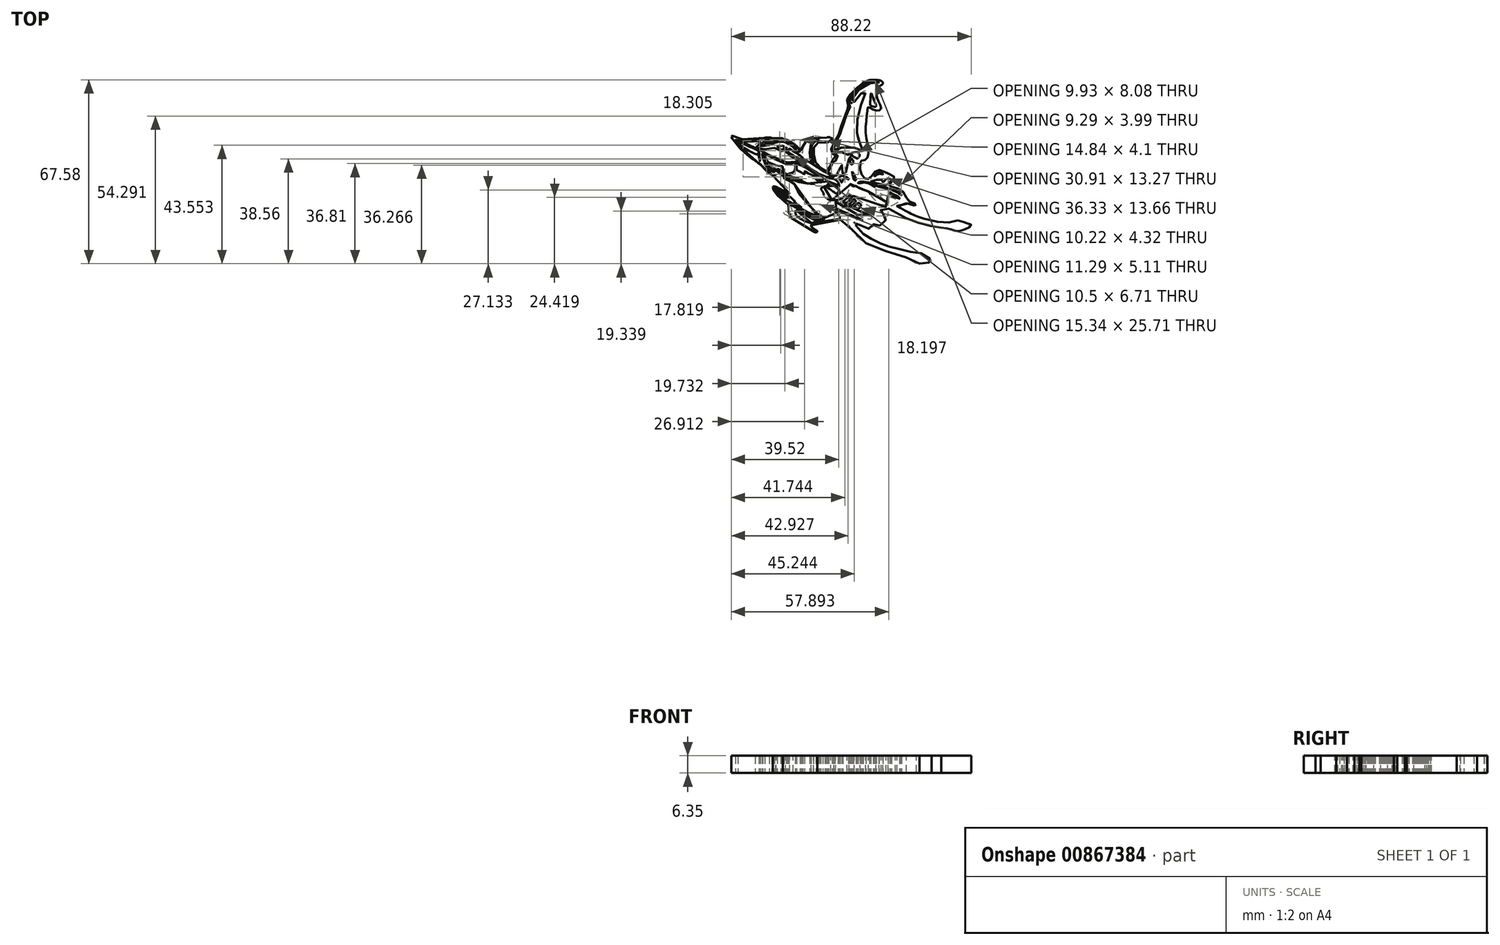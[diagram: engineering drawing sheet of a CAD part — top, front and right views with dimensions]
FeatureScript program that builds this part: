
annotation { "Feature Type Name" : "Feature", "Feature Type Description" : "" }
export const myFeature = defineFeature(function(context is Context, id is Id, definition is map)
    precondition{}
    {
        {
            var Q0;
            Q0=qCreatedBy(makeId("Top.planeOp"),FACE);
            var sketch = newSketch(context, id + "F0", { "sketchPlane" : qUnion([Q0])});
            skFitSpline(sketch, "E0", {"points": [v(41.98, 48.6) * mm, v(43.9, 48.97) * mm, v(44.37, 48.91) * mm, v(44.52, 48.63) * mm, v(44.44, 48.26) * mm, v(44.15, 47.9) * mm, v(43.74, 47.62) * mm, v(42.93, 47.19) * mm, v(42.29, 46.82) * mm, v(42.06, 46.82) * mm, v(40.95, 46.8) * mm, v(39.6, 46.76) * mm, v(38.49, 46.64) * mm, v(38.07, 46.36) * mm, v(37.56, 45.85) * mm, v(37.26, 45.35) * mm, v(37.13, 44.9) * mm, v(37.04, 44.36) * mm, v(37.01, 43.72) * mm, v(37, 42.9) * mm, v(37.17, 41.97) * mm, v(37.41, 41.22) * mm, v(37.56, 40.41) * mm, v(37.68, 39.64) * mm, v(37.94, 38.93) * mm, v(38.5, 38.27) * mm, v(39.2, 37.71) * mm, v(39.97, 37.17) * mm, v(40.53, 36.8) * mm, v(41.1, 36.43) * mm, v(41.55, 36.15) * mm, v(41.7, 36.05) * mm, v(41.86, 36.05) * mm, v(41.98, 36.19) * mm, v(42.32, 36.67) * mm, v(43.09, 38) * mm, v(43.48, 38.84) * mm, v(43.73, 39.67) * mm, v(43.85, 40.2) * mm, v(43.95, 40.42) * mm, v(44.07, 40.53) * mm, v(44.25, 40.59) * mm, v(44.44, 40.57) * mm, v(44.68, 40.66) * mm, v(44.9, 40.88) * mm, v(45.08, 41.2) * mm, v(45.14, 41.5) * mm, v(45.1, 41.77) * mm, v(44.95, 42.01) * mm, v(44.72, 42.23) * mm, v(44.54, 42.34) * mm, v(44.36, 42.38) * mm, v(44.25, 42.44) * mm, v(44, 42.65) * mm, v(43.84, 42.84) * mm, v(43.48, 43.12) * mm, v(43.35, 43.2) * mm, v(43.39, 43.45) * mm, v(43.48, 43.85) * mm, v(43.57, 44.25) * mm, v(44.01, 45.4) * mm, v(44.39, 46.2) * mm, v(44.73, 46.9) * mm, v(45.15, 47.64) * mm, v(45.68, 48.6) * mm, v(46.04, 49.27) * mm, v(46.33, 49.92) * mm, v(46.48, 50.56) * mm, v(46.91, 51.88) * mm, v(47.29, 52.96) * mm, v(47.67, 53.81) * mm, v(48.05, 54.9) * mm, v(48.34, 55.82) * mm, v(48.7, 56.96) * mm, v(49.23, 58.28) * mm, v(49.6, 59.15) * mm, v(49.93, 59.76) * mm, v(50.1, 60.04) * mm, v(50.13, 60.13) * mm, v(50.08, 60.23) * mm, v(49.9, 60.42) * mm, v(49.81, 60.56) * mm, v(49.53, 60.97) * mm, v(49.44, 61.13) * mm, v(49.4, 61.27) * mm, v(49.36, 61.68) * mm, v(49.37, 62.12) * mm, v(49.38, 62.52) * mm, v(49.48, 62.86) * mm, v(49.7, 63.3) * mm, v(50.14, 63.88) * mm, v(50.55, 64.34) * mm, v(51.4, 65.2) * mm, v(52.13, 65.94) * mm, v(52.85, 66.69) * mm, v(53.39, 67.22) * mm, v(53.94, 67.76) * mm, v(54.36, 68.08) * mm, v(55.06, 68.47) * mm], "startDerivative": vector(117.58, 26) * mm, "endDerivative": vector(61.76, 33.34) * mm});
            skFitSpline(sketch, "E1", {"points": [v(55.06, 68.47) * mm, v(55.59, 68.8) * mm, v(56.05, 69.09) * mm, v(56.53, 69.34) * mm, v(57.02, 69.52) * mm, v(57.43, 69.66) * mm, v(57.78, 69.7) * mm, v(58.18, 69.74) * mm, v(58.9, 69.73) * mm, v(59.55, 69.72) * mm, v(60.32, 69.7) * mm, v(61.28, 69.62) * mm, v(61.67, 69.5) * mm, v(61.99, 69.32) * mm, v(62.26, 69.08) * mm, v(62.43, 68.88) * mm, v(62.5, 68.77) * mm, v(62.52, 68.62) * mm, v(62.52, 68.43) * mm, v(62.48, 68.3) * mm, v(62.4, 68.17) * mm, v(62.22, 68.02) * mm, v(62.06, 67.9) * mm, v(61.9, 67.8) * mm, v(61.7, 67.69) * mm, v(61.54, 67.59) * mm, v(61.4, 67.5) * mm, v(61.17, 67.37) * mm, v(61, 67.26) * mm, v(60.79, 67.13) * mm, v(60.6, 66.97) * mm, v(60.47, 66.85) * mm, v(60.3, 66.68) * mm, v(60.16, 66.48) * mm, v(60.08, 66.3) * mm, v(60, 66.01) * mm], "startDerivative": vector(13.49, 8.7) * mm, "endDerivative": vector(-3.18, -11.09) * mm});
            skFitSpline(sketch, "E2", {"points": [v(58.3, 64.82) * mm, v(58.43, 64.52) * mm, v(58.67, 63.82) * mm, v(58.93, 63.08) * mm, v(59.33, 62) * mm, v(59.67, 61.3) * mm, v(60.07, 60.52) * mm, v(60.14, 60.21) * mm, v(60, 59.97) * mm, v(59.8, 59.88) * mm, v(59.3, 59.86) * mm, v(58.85, 59.98) * mm, v(58.4, 60.17) * mm, v(57.95, 60.44) * mm, v(57.82, 60.59) * mm, v(57.78, 60.94) * mm, v(57.9, 61.76) * mm, v(57.96, 62.72) * mm, v(58, 63.73) * mm, v(58.07, 64.4) * mm, v(58.14, 64.66) * mm, v(58.18, 64.78) * mm, v(58.3, 64.82) * mm]});
            skFitSpline(sketch, "E3", {"points": [v(55.21, 43.64) * mm, v(55.24, 44.2) * mm, v(55.08, 44.77) * mm, v(54.83, 45.45) * mm, v(54.48, 46.03) * mm, v(54.03, 46.77) * mm, v(53.69, 47.3) * mm, v(53.4, 47.93) * mm, v(53.24, 48.48) * mm, v(53.13, 49.1) * mm, v(53, 49.95) * mm, v(52.96, 50.59) * mm, v(52.92, 52.06) * mm, v(52.93, 53.55) * mm, v(53.06, 54.95) * mm, v(53.33, 56.48) * mm, v(53.76, 58.41) * mm, v(54.17, 59.75) * mm, v(54.6, 60.97) * mm, v(55.07, 62.3) * mm, v(55.72, 63.92) * mm, v(55.96, 64.35) * mm, v(56.2, 65.04) * mm, v(56.3, 65.47) * mm, v(56.27, 65.67) * mm, v(56.04, 65.75) * mm, v(55.8, 65.66) * mm, v(55.4, 65.43) * mm, v(54.82, 65.01) * mm, v(54.12, 64.39) * mm, v(53.53, 63.73) * mm, v(52.83, 62.85) * mm, v(52.33, 62.13) * mm, v(51.81, 61.5) * mm, v(51.34, 61.23) * mm, v(51.06, 61.18) * mm, v(50.84, 61.28) * mm, v(50.71, 61.48) * mm, v(50.84, 61.87) * mm, v(51.09, 62.32) * mm, v(51.48, 62.95) * mm, v(51.94, 63.63) * mm, v(52.34, 64.22) * mm, v(53.1, 65.33) * mm, v(53.88, 66.29) * mm, v(54.81, 67.24) * mm, v(55.98, 68.08) * mm, v(56.93, 68.42) * mm, v(58.16, 68.54) * mm, v(59.23, 68.55) * mm, v(59.7, 68.46) * mm, v(60.42, 68.52) * mm, v(60.87, 68.66) * mm, v(61.08, 68.76) * mm, v(61.08, 68.88) * mm, v(60.98, 69.01) * mm, v(60.39, 69.17) * mm, v(59.5, 69.32) * mm, v(58.18, 69.2) * mm, v(57.02, 68.88) * mm, v(55.92, 68.46) * mm, v(55.55, 68.26) * mm, v(54.99, 67.95) * mm, v(54.67, 67.72) * mm, v(53.94, 67.13) * mm, v(53.3, 66.48) * mm, v(52.68, 65.85) * mm, v(52.02, 65.17) * mm, v(51.74, 64.88) * mm, v(51.09, 64.15) * mm, v(50.5, 63.44) * mm, v(50.11, 62.82) * mm, v(49.98, 62.5) * mm, v(49.87, 61.78) * mm, v(49.9, 61.38) * mm, v(50, 61.1) * mm, v(50.54, 60.42) * mm, v(50.67, 60.13) * mm, v(50.67, 60.03) * mm, v(50.54, 59.88) * mm, v(50.3, 59.58) * mm, v(50.12, 59.3) * mm, v(49.73, 58.28) * mm, v(49.36, 57.33) * mm, v(48.91, 56.23) * mm, v(48.62, 55.32) * mm, v(48.36, 54.43) * mm, v(48.13, 53.78) * mm, v(47.8, 52.92) * mm, v(47.33, 51.68) * mm, v(47.02, 50.78) * mm, v(46.82, 49.96) * mm, v(46.32, 48.78) * mm, v(45.52, 47.37) * mm, v(45.1, 46.63) * mm, v(44.52, 45.44) * mm, v(44.04, 44.25) * mm, v(43.86, 43.45) * mm, v(43.89, 43.32) * mm, v(44.04, 43.34) * mm, v(44.28, 43.54) * mm, v(44.6, 43.78) * mm, v(44.94, 44.05) * mm, v(45.78, 44.4) * mm, v(46.69, 44.7) * mm, v(47.67, 44.96) * mm, v(48.57, 45.13) * mm, v(49.81, 45.12) * mm, v(51.28, 44.99) * mm, v(52.27, 44.73) * mm, v(52.95, 44.55) * mm, v(53.91, 44.17) * mm, v(54.47, 43.9) * mm, v(54.86, 43.7) * mm, v(55.21, 43.64) * mm]});
            skFitSpline(sketch, "E4", {"points": [v(60, 66.01) * mm, v(60, 65.43) * mm, v(60.12, 64.57) * mm, v(60.24, 63.95) * mm, v(60.5, 63.08) * mm, v(60.74, 62.35) * mm, v(61.04, 61.6) * mm, v(61.36, 60.87) * mm, v(61.66, 60.16) * mm, v(61.9, 59.48) * mm, v(61.92, 58.98) * mm, v(61.64, 58.7) * mm, v(61.25, 58.5) * mm, v(60.88, 58.44) * mm, v(60.34, 58.47) * mm, v(60, 58.52) * mm, v(59.22, 58.76) * mm, v(58.39, 59.16) * mm, v(57.58, 59.55) * mm, v(57.16, 59.73) * mm, v(57.02, 59.74) * mm, v(56.94, 59.68) * mm, v(56.9, 59.39) * mm, v(56.86, 58.84) * mm, v(56.76, 58.05) * mm, v(56.64, 56.68) * mm, v(56.46, 55.36) * mm, v(56.33, 53.9) * mm, v(56.2, 51.87) * mm, v(56.23, 50.08) * mm, v(56.37, 48.56) * mm, v(56.61, 47.28) * mm, v(56.9, 46.13) * mm, v(57.16, 44.6) * mm, v(57.23, 43.04) * mm, v(57.13, 41.88) * mm, v(56.92, 41.26) * mm, v(56.44, 40.67) * mm, v(55.95, 40.28) * mm, v(55.33, 40.08) * mm, v(54.79, 40.06) * mm, v(54.31, 40.03) * mm, v(54.27, 39.86) * mm, v(54.24, 39.46) * mm], "startDerivative": vector(-1.15, -26.38) * mm, "endDerivative": vector(-2.88, -24.95) * mm});
            skFitSpline(sketch, "E5", {"points": [v(44.86, 43.01) * mm, v(45.21, 43.13) * mm, v(46.25, 43.18) * mm, v(47.33, 43.12) * mm, v(48.31, 42.85) * mm, v(49.12, 42.58) * mm, v(49.7, 42.26) * mm, v(49.8, 42.15) * mm, v(49.99, 42.17) * mm, v(50.36, 42.4) * mm, v(50.83, 42.7) * mm, v(51.4, 42.97) * mm, v(51.95, 43.15) * mm, v(52.44, 43.28) * mm, v(52.89, 43.32) * mm, v(53.4, 43.25) * mm, v(53.81, 42.92) * mm, v(54.04, 42.58) * mm, v(54.13, 42.24) * mm, v(54.13, 41.83) * mm, v(54, 41.42) * mm, v(53.81, 41.13) * mm, v(53.51, 40.92) * mm, v(53.22, 40.8) * mm, v(52.8, 40.8) * mm, v(52.45, 40.87) * mm, v(52.08, 41.07) * mm, v(51.78, 41.41) * mm, v(51.63, 41.75) * mm, v(51.59, 42.16) * mm, v(51.58, 42.39) * mm, v(51.53, 42.47) * mm, v(51.38, 42.43) * mm, v(51.17, 42.26) * mm, v(50.92, 42) * mm, v(50.7, 41.76) * mm, v(50.5, 41.5) * mm, v(50.32, 41.13) * mm, v(50.06, 40.52) * mm, v(49.85, 39.8) * mm, v(49.6, 38.88) * mm, v(49.44, 37.97) * mm, v(49.27, 37.05) * mm, v(49.1, 36.23) * mm, v(48.95, 35.73) * mm, v(48.74, 35.2) * mm, v(48.51, 35) * mm, v(48.18, 34.95) * mm, v(47.86, 35) * mm, v(47.61, 35.3) * mm, v(47.45, 35.68) * mm, v(47.39, 36.33) * mm, v(47.55, 36.93) * mm, v(47.7, 37.52) * mm, v(47.74, 38.07) * mm, v(47.65, 38.4) * mm, v(47.54, 38.47) * mm, v(47.3, 38.23) * mm, v(47, 37.62) * mm, v(46.66, 36.98) * mm, v(46.45, 36.58) * mm, v(46.14, 35.9) * mm, v(45.93, 35.5) * mm, v(45.56, 34.7) * mm, v(45.34, 34.25) * mm, v(45.25, 34.14) * mm, v(45.08, 34.16) * mm, v(44.82, 34.29) * mm, v(44.18, 34.6) * mm, v(43.57, 34.92) * mm, v(42.98, 35.27) * mm, v(42.57, 35.52) * mm, v(42.3, 35.7) * mm, v(42.23, 35.8) * mm, v(42.4, 36.05) * mm, v(42.79, 36.67) * mm, v(43.2, 37.4) * mm, v(43.55, 38.02) * mm, v(43.78, 38.44) * mm, v(43.9, 38.95) * mm, v(44.05, 39.41) * mm, v(44.17, 39.72) * mm, v(44.32, 39.9) * mm, v(44.54, 40) * mm, v(44.95, 40.03) * mm, v(45.32, 40.16) * mm, v(45.73, 40.56) * mm, v(45.97, 41.04) * mm, v(46, 41.53) * mm, v(45.9, 41.95) * mm, v(45.65, 42.38) * mm, v(45.3, 42.72) * mm, v(45.03, 42.88) * mm, v(44.86, 43.01) * mm]});
            skFitSpline(sketch, "E6", {"points": [v(50.81, 40.97) * mm, v(51.07, 40.76) * mm, v(51.37, 40.32) * mm, v(51.61, 39.93) * mm, v(51.69, 39.46) * mm, v(51.67, 39.07) * mm, v(51.53, 38.94) * mm, v(51.32, 38.76) * mm, v(51.13, 38.66) * mm, v(50.92, 38.66) * mm, v(50.7, 38.92) * mm, v(50.57, 39.35) * mm, v(50.53, 39.9) * mm, v(50.6, 40.38) * mm, v(50.65, 40.7) * mm, v(50.72, 40.9) * mm, v(50.81, 40.97) * mm]});
            skFitSpline(sketch, "E7", {"points": [v(51.25, 36.03) * mm, v(51.52, 35.68) * mm, v(51.85, 35.08) * mm, v(52.2, 34.41) * mm, v(52.5, 33.68) * mm, v(52.63, 33.3) * mm, v(52.63, 32.93) * mm, v(52.45, 32.8) * mm, v(52.26, 32.8) * mm, v(52.02, 32.85) * mm, v(51.83, 33.1) * mm, v(51.67, 33.49) * mm, v(51.56, 34.07) * mm, v(51.44, 34.7) * mm, v(51.33, 35.4) * mm, v(51.2, 35.86) * mm, v(51.25, 36.03) * mm]});
            skFitSpline(sketch, "E8", {"points": [v(46.22, 33.81) * mm, v(46.48, 34.06) * mm, v(47.08, 34.34) * mm, v(47.61, 34.4) * mm, v(48.35, 34.27) * mm, v(49.08, 34.03) * mm, v(49.44, 33.87) * mm, v(49.78, 33.56) * mm, v(49.92, 33.35) * mm, v(49.98, 33.17) * mm, v(49.94, 33.1) * mm, v(49.73, 33.22) * mm, v(49.44, 33.41) * mm, v(49.06, 33.55) * mm, v(48.57, 33.54) * mm, v(48.2, 33.39) * mm, v(47.94, 33.18) * mm, v(47.7, 32.85) * mm, v(47.55, 32.49) * mm, v(47.55, 32.24) * mm, v(47.45, 32) * mm, v(47.32, 32) * mm, v(47.23, 32.2) * mm, v(47.13, 32.44) * mm, v(46.97, 32.71) * mm, v(46.77, 32.98) * mm, v(46.5, 33.33) * mm, v(46.31, 33.53) * mm, v(46.23, 33.65) * mm, v(46.22, 33.81) * mm]});
            skFitSpline(sketch, "E9", {"points": [v(54.24, 39.46) * mm, v(54.15, 38.57) * mm, v(54.15, 37.55) * mm, v(54.18, 36.68) * mm, v(54.28, 36.16) * mm, v(54.38, 35.7) * mm, v(54.6, 35.16) * mm, v(54.87, 34.66) * mm, v(55.14, 34.25) * mm, v(55.43, 33.9) * mm, v(55.8, 33.52) * mm, v(56.14, 33.2) * mm, v(56.34, 33.08) * mm, v(56.63, 33.06) * mm, v(56.99, 33.18) * mm, v(57.36, 33.36) * mm, v(57.65, 33.6) * mm, v(57.9, 33.82) * mm, v(58.14, 34.08) * mm, v(58.53, 34.57) * mm, v(58.91, 35.13) * mm, v(59.3, 35.63) * mm, v(59.66, 35.98) * mm, v(60.1, 36.33) * mm, v(60.5, 36.52) * mm, v(60.94, 36.62) * mm, v(61.36, 36.64) * mm, v(61.97, 36.59) * mm, v(62.68, 36.27) * mm, v(63.08, 35.94) * mm, v(63.41, 35.53) * mm, v(63.58, 35.32) * mm, v(63.92, 35.33) * mm, v(64.34, 35.3) * mm, v(65.05, 35.06) * mm, v(65.74, 34.72) * mm, v(66.5, 34.3) * mm, v(67, 33.89) * mm, v(67.08, 33.75) * mm, v(66.99, 33.52) * mm, v(66.74, 33.25) * mm, v(66.37, 32.84) * mm, v(65.95, 32.42) * mm, v(65.5, 31.97) * mm, v(65.02, 31.47) * mm, v(64.74, 31.17) * mm, v(64.49, 30.88) * mm, v(64.8, 30.76) * mm, v(65.16, 30.68) * mm, v(65.52, 30.56) * mm, v(66.57, 30.26) * mm, v(67.8, 29.87) * mm, v(68.68, 29.57) * mm, v(69.76, 28.8) * mm, v(70.46, 27.9) * mm, v(70.97, 27.09) * mm, v(71.18, 26.64) * mm, v(71.22, 25.86) * mm, v(71.26, 25.5) * mm, v(71.7, 25.25) * mm, v(72.42, 25.06) * mm, v(73.1, 24.8) * mm, v(73.9, 24.47) * mm, v(74.63, 24.01) * mm, v(74.83, 23.66) * mm, v(74.78, 23.48) * mm, v(74.47, 23.4) * mm, v(74.18, 23.48) * mm, v(73.5, 23.73) * mm, v(72.82, 23.95) * mm, v(71.9, 24.2) * mm, v(71.09, 24.27) * mm, v(70.46, 24.07) * mm, v(69.71, 23.82) * mm, v(69.02, 23.64) * mm, v(68.47, 23.53) * mm, v(68.09, 23.45) * mm, v(67.8, 23.4) * mm, v(67.73, 23.35) * mm, v(67.95, 23.15) * mm, v(68.29, 22.98) * mm, v(68.61, 22.85) * mm, v(68.96, 22.7) * mm], "startDerivative": vector(-7.45, -55.61) * mm, "endDerivative": vector(33.73, -15.96) * mm});
            skFitSpline(sketch, "E10", {"points": [v(60.87, 35.68) * mm, v(61.14, 35.7) * mm, v(61.66, 35.69) * mm, v(62.06, 35.58) * mm, v(62.32, 35.45) * mm, v(62.48, 35.27) * mm, v(62.57, 35.13) * mm, v(62.55, 34.97) * mm, v(62.34, 34.98) * mm, v(62.04, 35.1) * mm, v(61.66, 35.19) * mm, v(61.2, 35.19) * mm, v(60.85, 35.1) * mm, v(60.52, 34.97) * mm, v(60.24, 34.81) * mm, v(60.02, 34.66) * mm, v(59.78, 34.5) * mm, v(59.58, 34.37) * mm, v(59.4, 34.33) * mm, v(59.4, 34.44) * mm, v(59.61, 34.74) * mm, v(59.9, 35.07) * mm, v(60.13, 35.33) * mm, v(60.36, 35.5) * mm, v(60.64, 35.63) * mm, v(60.87, 35.68) * mm]});
            skFitSpline(sketch, "E11", {"points": [v(63.93, 31.08) * mm, v(64.34, 31.44) * mm, v(64.74, 31.82) * mm, v(65.27, 32.34) * mm, v(65.6, 32.69) * mm, v(65.74, 32.87) * mm, v(65.72, 33.05) * mm, v(65.49, 33.21) * mm, v(65.23, 33.34) * mm, v(64.88, 33.44) * mm, v(64.56, 33.48) * mm, v(64.16, 33.46) * mm, v(63.85, 33.36) * mm, v(63.55, 33.12) * mm, v(63.32, 32.86) * mm, v(63.12, 32.57) * mm, v(63, 32.34) * mm, v(62.84, 32.21) * mm, v(62.67, 32.16) * mm, v(62.46, 32.2) * mm, v(62.33, 32.3) * mm, v(62.25, 32.5) * mm, v(62.23, 32.76) * mm, v(62.2, 32.92) * mm, v(62.14, 33.01) * mm, v(62.05, 33.08) * mm, v(61.79, 33.11) * mm, v(61.26, 33.1) * mm, v(60.51, 33) * mm, v(59.83, 32.87) * mm, v(59.18, 32.73) * mm, v(58.5, 32.56) * mm, v(58.1, 32.46) * mm, v(58.09, 32.37) * mm, v(58.58, 32.14) * mm, v(59.28, 31.94) * mm, v(60.2, 31.7) * mm, v(61.37, 31.47) * mm, v(62.18, 31.3) * mm, v(63.15, 31.11) * mm, v(63.64, 31.04) * mm, v(63.93, 31.08) * mm]});
            skFitSpline(sketch, "E12", {"points": [v(53.59, 32) * mm, v(54.05, 32.18) * mm, v(54.66, 32.3) * mm, v(55.39, 32.32) * mm, v(56.1, 32.25) * mm, v(56.91, 32.09) * mm, v(57.75, 31.89) * mm, v(58.38, 31.66) * mm, v(58.82, 31.43) * mm, v(59.19, 31.12) * mm, v(59.44, 30.81) * mm, v(59.6, 30.56) * mm, v(59.67, 30.37) * mm, v(59.66, 30.27) * mm, v(59.5, 30.32) * mm, v(59.24, 30.48) * mm, v(58.9, 30.73) * mm, v(58.59, 30.96) * mm, v(58.16, 31.23) * mm, v(57.73, 31.46) * mm, v(57.2, 31.72) * mm, v(56.68, 31.86) * mm, v(56.17, 31.98) * mm, v(55.66, 31.97) * mm, v(55, 31.9) * mm, v(54.47, 31.84) * mm, v(54, 31.76) * mm, v(53.57, 31.76) * mm, v(53.4, 31.77) * mm, v(53.4, 31.86) * mm, v(53.5, 31.95) * mm, v(53.59, 32) * mm]});
            skFitSpline(sketch, "E13", {"points": [v(61.98, 30.88) * mm, v(62.53, 30.68) * mm, v(63.48, 30.25) * mm, v(64.45, 29.88) * mm, v(65.55, 29.53) * mm, v(66.52, 29.22) * mm, v(67.54, 28.85) * mm, v(68.43, 28.35) * mm, v(69.24, 27.61) * mm, v(69.46, 27.34) * mm, v(69.4, 27.26) * mm, v(69.3, 27.33) * mm, v(68.99, 27.59) * mm, v(68.45, 28.01) * mm, v(67.6, 28.48) * mm, v(66.86, 28.82) * mm, v(66.04, 29.17) * mm, v(65.1, 29.47) * mm, v(63.89, 29.8) * mm, v(62.47, 30.13) * mm, v(61.5, 30.32) * mm, v(60.75, 30.53) * mm, v(60.16, 30.82) * mm, v(59.79, 31.2) * mm, v(59.74, 31.3) * mm, v(59.8, 31.34) * mm, v(59.94, 31.3) * mm, v(60.38, 31.2) * mm, v(60.84, 31.1) * mm, v(61.33, 30.99) * mm, v(61.67, 30.92) * mm, v(61.98, 30.88) * mm]});
            skFitSpline(sketch, "E14", {"points": [v(65.16, 28.5) * mm, v(65.96, 27.97) * mm, v(67.04, 27.39) * mm, v(67.93, 26.89) * mm, v(68.38, 26.56) * mm, v(68.66, 26.3) * mm, v(68.7, 26.13) * mm, v(68.66, 26.07) * mm, v(68.32, 26.14) * mm, v(67.68, 26.38) * mm, v(66.93, 26.62) * mm, v(66.4, 26.83) * mm, v(65.92, 27) * mm, v(65.68, 27.15) * mm, v(65.6, 27.29) * mm, v(65.6, 27.47) * mm, v(65.49, 27.68) * mm, v(65.3, 27.99) * mm, v(65.14, 28.24) * mm, v(65.08, 28.4) * mm, v(65.08, 28.5) * mm, v(65.16, 28.5) * mm]});
            skFitSpline(sketch, "E15", {"points": [v(68.96, 22.7) * mm, v(70.34, 21.9) * mm, v(71.26, 21.4) * mm, v(71.97, 21.01) * mm, v(72.2, 20.89) * mm, v(72.35, 20.9) * mm, v(72.53, 20.78) * mm, v(72.7, 20.61) * mm, v(73.1, 20.4) * mm, v(73.96, 20) * mm, v(74.59, 19.8) * mm, v(75.13, 19.62) * mm, v(76.54, 19.04) * mm, v(78.45, 18.56) * mm, v(80.4, 18.1) * mm, v(82.93, 17.54) * mm, v(84.5, 17.4) * mm, v(86.23, 17.26) * mm, v(87.16, 17.34) * mm, v(88.08, 17.6) * mm, v(88.64, 17.84) * mm, v(89.86, 18.02) * mm, v(90.93, 17.87) * mm, v(92.44, 17.43) * mm, v(93.45, 17.02) * mm, v(94.23, 16.75) * mm, v(94.78, 16.58) * mm, v(95, 16.41) * mm, v(94.85, 15.95) * mm, v(94.35, 15.52) * mm, v(93.77, 15.23) * mm, v(92.86, 14.86) * mm, v(92.06, 14.56) * mm, v(91.47, 14.37) * mm, v(91.21, 14.26) * mm, v(90.85, 14.17) * mm, v(90.09, 14.13) * mm, v(89.46, 14.23) * mm, v(88.88, 14.33) * mm, v(88.2, 14.53) * mm, v(87.35, 14.8) * mm, v(86.53, 15.02) * mm, v(85.06, 15.24) * mm, v(84.02, 15.41) * mm], "startDerivative": vector(45.45, -25.8) * mm, "endDerivative": vector(-37.02, 6.77) * mm});
            skFitSpline(sketch, "E16", {"points": [v(84.02, 15.41) * mm, v(83.3, 15.55) * mm, v(82.43, 15.67) * mm, v(81.58, 15.79) * mm, v(80.7, 15.96) * mm, v(79.63, 16.18) * mm, v(78.68, 16.38) * mm, v(77.84, 16.57) * mm, v(76.3, 16.99) * mm, v(74.77, 17.52) * mm, v(73.68, 17.88) * mm, v(72.4, 18.4) * mm, v(71.03, 18.92) * mm, v(70.3, 19.27) * mm, v(69.31, 19.76) * mm, v(68.4, 20.35) * mm, v(67.86, 20.67) * mm, v(67.24, 21.09) * mm, v(66.49, 21.57) * mm, v(65.87, 21.92) * mm, v(65.24, 22.23) * mm, v(64.84, 22.4) * mm, v(64.65, 22.44) * mm, v(64.19, 22.4) * mm, v(63.76, 22.3) * mm, v(63.32, 22.23) * mm, v(62.85, 22.11) * mm, v(62.12, 21.93) * mm, v(61.65, 21.83) * mm, v(61.37, 21.74) * mm, v(61.17, 21.7) * mm, v(61.14, 21.64) * mm, v(61.32, 21.53) * mm, v(61.72, 21.3) * mm, v(62.14, 21.06) * mm, v(62.58, 20.79) * mm, v(62.94, 20.52) * mm, v(63.32, 20.09) * mm, v(63.57, 19.56) * mm, v(63.71, 19.02) * mm, v(63.71, 18.47) * mm, v(63.53, 18.05) * mm, v(63.24, 17.67) * mm, v(62.75, 17.08) * mm, v(62.41, 16.74) * mm, v(61.97, 16.42) * mm, v(61.58, 16.23) * mm, v(61.28, 16.2) * mm, v(60.89, 16.22) * mm, v(60.54, 16.32) * mm, v(60.2, 16.43) * mm, v(59.8, 16.56) * mm, v(59.56, 16.63) * mm, v(59.37, 16.68) * mm, v(59.16, 16.67) * mm, v(59.1, 16.64) * mm, v(59.02, 16.52) * mm, v(58.28, 15.24) * mm, v(58.02, 14.85) * mm, v(57.94, 14.76) * mm, v(57.8, 14.76) * mm, v(57.64, 14.82) * mm, v(57.36, 14.95) * mm, v(56.93, 15.13) * mm, v(55.29, 15.84) * mm, v(54.4, 16.27) * mm, v(52.88, 16.9) * mm, v(52.42, 17.13) * mm, v(52.16, 17.22) * mm, v(52.06, 17.24) * mm, v(52.03, 17.16) * mm, v(52.13, 17.03) * mm, v(52.26, 16.82) * mm, v(52.43, 16.5) * mm, v(52.63, 16.15) * mm, v(53.22, 15.2) * mm, v(53.77, 14.6) * mm, v(54.45, 13.9) * mm, v(55.06, 13.28) * mm, v(55.6, 12.78) * mm, v(56, 12.45) * mm, v(56.53, 12.19) * mm, v(57.3, 11.8) * mm, v(58.07, 11.42) * mm, v(58.97, 10.97) * mm, v(59.8, 10.53) * mm, v(60.58, 10.12) * mm, v(61.25, 9.82) * mm, v(61.89, 9.51) * mm, v(62.09, 9.49) * mm, v(62.35, 9.36) * mm, v(63.41, 8.94) * mm, v(64.16, 8.7) * mm, v(64.9, 8.46) * mm, v(65.29, 8.48) * mm, v(65.97, 8.25) * mm, v(66.53, 8.1) * mm, v(67.77, 7.75) * mm, v(68.63, 7.45) * mm, v(69.86, 7.11) * mm, v(70.9, 6.85) * mm, v(71.8, 6.67) * mm, v(72.57, 6.55) * mm, v(73.45, 6.52) * mm, v(74.3, 6.52) * mm, v(75.16, 6.39) * mm, v(75.92, 6.2) * mm, v(76.93, 5.88) * mm, v(78.18, 5.43) * mm, v(78.61, 5.2) * mm, v(79.16, 4.66) * mm, v(79.59, 4.24) * mm, v(79.9, 3.95) * mm, v(80.18, 3.8) * mm, v(80.36, 3.59) * mm, v(80.4, 3.46) * mm, v(80.4, 3.24) * mm, v(80.29, 3.06) * mm, v(79.9, 2.73) * mm, v(79.4, 2.51) * mm, v(78.94, 2.38) * mm, v(78.53, 2.3) * mm, v(77.9, 2.24) * mm, v(76.8, 2.2) * mm, v(76.06, 2.17) * mm], "startDerivative": vector(-77.84, 16.14) * mm, "endDerivative": vector(-75.6, -1.17) * mm});
            skFitSpline(sketch, "E17", {"points": [v(76.06, 2.17) * mm, v(75.27, 2.17) * mm, v(75, 2.17) * mm, v(74.67, 2.34) * mm, v(74.31, 2.49) * mm, v(73.87, 2.64) * mm, v(73.5, 2.89) * mm, v(72.98, 3.26) * mm, v(72.65, 3.5) * mm, v(72.18, 3.78) * mm, v(71.67, 4.07) * mm, v(71.27, 4.34) * mm, v(70.6, 4.66) * mm, v(70.04, 4.93) * mm, v(68.62, 5.42) * mm, v(67.83, 5.63) * mm, v(66.96, 5.86) * mm, v(65.24, 6.33) * mm, v(64.7, 6.48) * mm, v(64.4, 6.62) * mm, v(63.5, 6.83) * mm, v(62.48, 7.12) * mm, v(61.42, 7.47) * mm, v(60.6, 7.75) * mm, v(59.11, 8.3) * mm, v(58.24, 8.73) * mm, v(57.62, 8.95) * mm, v(56.74, 9.44) * mm, v(56.02, 9.87) * mm, v(55.2, 10.35) * mm, v(54.68, 10.7) * mm, v(54.26, 11.02) * mm, v(53.26, 11.94) * mm, v(52.84, 12.36) * mm, v(52.33, 12.93) * mm, v(51.77, 13.73) * mm, v(51.24, 14.5) * mm, v(50.7, 15.44) * mm, v(50.37, 16.05) * mm, v(49.9, 16.95) * mm, v(49.58, 17.49) * mm, v(49.27, 17.95) * mm, v(49.08, 18.17) * mm, v(48.76, 18.32) * mm, v(48.5, 18.4) * mm, v(48.15, 18.4) * mm, v(47.34, 18.36) * mm, v(46.6, 18.26) * mm, v(45.46, 18.08) * mm, v(44.44, 17.92) * mm, v(40.42, 17.26) * mm, v(37.97, 16.73) * mm, v(36.37, 16.45) * mm, v(36.13, 16.34) * mm, v(36.07, 16.26) * mm, v(36.08, 16.07) * mm, v(36.3, 15.73) * mm, v(36.69, 15.35) * mm, v(37.34, 14.82) * mm, v(37.8, 14.5) * mm, v(38.12, 14.33) * mm, v(38.36, 14.14) * mm, v(38.4, 13.99) * mm, v(38.35, 13.85) * mm, v(38.24, 13.78) * mm, v(38, 13.7) * mm, v(37.8, 13.67) * mm, v(37.47, 13.75) * mm, v(37.15, 13.97) * mm, v(36.81, 14.2) * mm, v(36.43, 14.45) * mm, v(35.77, 14.82) * mm, v(35.18, 15.16) * mm, v(33.49, 16.1) * mm, v(32, 16.97) * mm, v(28.81, 18.99) * mm, v(27.7, 19.64) * mm, v(26.31, 20.46) * mm, v(25.87, 20.97) * mm, v(25.72, 21.38) * mm, v(25.76, 21.66) * mm, v(26.08, 21.74) * mm, v(26.5, 21.63) * mm, v(27.05, 21.31) * mm, v(27.57, 21.06) * mm, v(28.14, 20.79) * mm, v(28.64, 20.57) * mm, v(29.13, 20.38) * mm, v(29.4, 20.31) * mm, v(29.5, 20.4) * mm, v(29.47, 20.65) * mm, v(29.42, 21.02) * mm, v(29.32, 21.48) * mm, v(29.17, 21.98) * mm, v(28.93, 22.74) * mm, v(28.56, 23.21) * mm, v(27.87, 23.65) * mm, v(26.89, 24.2) * mm, v(26.12, 24.7) * mm, v(25.96, 24.9) * mm, v(25.98, 25.07) * mm, v(26.13, 25.16) * mm, v(26.44, 25.03) * mm, v(26.66, 24.92) * mm, v(26.76, 24.91) * mm, v(26.78, 24.94) * mm, v(26.76, 25) * mm, v(26.7, 25.05) * mm, v(26.54, 25.13) * mm, v(26, 25.49) * mm, v(25.58, 25.73) * mm, v(25.08, 26.1) * mm, v(24.73, 26.39) * mm, v(24.08, 27) * mm, v(23.1, 28.08) * mm, v(22.5, 28.88) * mm, v(22.14, 29.56) * mm, v(22.04, 30.15) * mm, v(22.13, 30.44) * mm, v(22.45, 30.57) * mm, v(22.81, 30.55) * mm, v(23.38, 30.36) * mm, v(23.75, 30.14) * mm, v(24.13, 29.94) * mm, v(24.72, 29.67) * mm, v(25.4, 29.3) * mm, v(25.88, 29.03) * mm, v(26.25, 28.9) * mm, v(26.65, 28.6) * mm, v(27.28, 28.3) * mm, v(27.7, 28.05) * mm, v(27.98, 27.93) * mm, v(28.15, 27.95) * mm, v(28.25, 28.13) * mm, v(28.3, 28.34) * mm, v(28.19, 28.77) * mm, v(28, 29.29) * mm, v(27.84, 29.57) * mm, v(27.52, 29.9) * mm, v(26.64, 30.57) * mm, v(26, 31.02) * mm, v(25.46, 31.4) * mm, v(24.9, 31.8) * mm, v(24.02, 32.49) * mm, v(23.5, 32.95) * mm, v(23.12, 33.44) * mm, v(23, 33.67) * mm, v(23, 33.94) * mm, v(23.11, 34.31) * mm, v(23.22, 34.61) * mm, v(23.28, 34.82) * mm, v(23.3, 34.97) * mm, v(23.26, 35.02) * mm, v(23.11, 34.97) * mm, v(22.86, 34.85) * mm, v(22.47, 34.8) * mm, v(22.04, 34.76) * mm, v(21.6, 34.81) * mm, v(21.12, 35.03) * mm, v(20.67, 35.35) * mm, v(20.08, 35.84) * mm, v(19.68, 36.25) * mm, v(19, 36.97) * mm, v(18.53, 37.6) * mm, v(18.15, 38.1) * mm, v(17.93, 38.3) * mm, v(17.6, 38.54) * mm, v(16.38, 39.41) * mm, v(15.27, 40.2) * mm, v(13.94, 41.17) * mm, v(11.87, 42.9) * mm, v(9.37, 45.3) * mm, v(8.23, 46.7) * mm, v(7.54, 47.63) * mm, v(6.92, 48.66) * mm, v(6.79, 49) * mm, v(6.8, 49.14) * mm, v(7.06, 49.2) * mm, v(7.4, 49.16) * mm, v(7.81, 49) * mm, v(8.29, 48.8) * mm, v(9.95, 48.25) * mm, v(11.15, 47.83) * mm, v(12.02, 47.6) * mm, v(13.17, 47.48) * mm, v(14.13, 47.45) * mm, v(15.25, 47.45) * mm, v(16.11, 47.58) * mm, v(16.97, 47.8) * mm, v(18.1, 48.18) * mm, v(18.92, 48.44) * mm, v(19.67, 48.55) * mm, v(20.22, 48.57) * mm, v(20.64, 48.57) * mm, v(21.15, 48.5) * mm, v(22, 48.26) * mm, v(22.65, 48.04) * mm, v(23.1, 48.05) * mm, v(23.68, 48.2) * mm, v(25.04, 48.25) * mm, v(26.47, 48.24) * mm, v(27.51, 47.95) * mm, v(28.7, 47.36) * mm, v(29.88, 46.56) * mm, v(30.68, 45.88) * mm, v(31.53, 45.05) * mm, v(32.18, 44.25) * mm, v(32.56, 43.57) * mm, v(32.84, 43.02) * mm, v(32.97, 42.78) * mm, v(33.04, 42.75) * mm, v(33.08, 42.94) * mm, v(33.11, 43.56) * mm, v(33.26, 44.5) * mm, v(33.57, 45.73) * mm, v(33.86, 46.76) * mm, v(34.5, 47.82) * mm, v(35.91, 48.82) * mm, v(37.29, 49.16) * mm, v(38.17, 49.11) * mm, v(39.02, 49.02) * mm, v(39.87, 48.73) * mm, v(40.46, 48.61) * mm, v(41, 48.55) * mm, v(41.62, 48.58) * mm, v(41.98, 48.6) * mm, v(42.72, 48.76) * mm], "startDerivative": vector(-184.6, 4.05) * mm, "endDerivative": vector(172.05, 43.36) * mm});
            skFitSpline(sketch, "E18", {"points": [v(38.37, 47.61) * mm, v(37.53, 47.45) * mm, v(36.93, 47.25) * mm, v(36.44, 46.9) * mm, v(36.12, 46.3) * mm, v(35.86, 45.48) * mm, v(35.73, 44.34) * mm, v(35.66, 43.63) * mm, v(35.63, 42.47) * mm, v(35.86, 41.15) * mm, v(36.02, 40.43) * mm, v(36.23, 39.85) * mm, v(36.49, 39.47) * mm, v(36.84, 39.13) * mm, v(37.02, 39.05) * mm, v(37.07, 39.23) * mm, v(37.02, 39.65) * mm, v(36.87, 40.35) * mm, v(36.8, 40.72) * mm, v(36.63, 41.37) * mm, v(36.4, 42.08) * mm, v(36.22, 42.8) * mm, v(36.2, 43.93) * mm, v(36.24, 44.72) * mm, v(36.44, 45.58) * mm, v(36.75, 46.23) * mm, v(37.2, 46.77) * mm, v(37.66, 47.1) * mm, v(38.04, 47.3) * mm, v(38.5, 47.45) * mm, v(38.93, 47.5) * mm, v(39.06, 47.54) * mm, v(38.97, 47.61) * mm, v(38.72, 47.62) * mm, v(38.37, 47.61) * mm]});
            skFitSpline(sketch, "E19", {"points": [v(24.25, 47.76) * mm, v(26.08, 47.77) * mm, v(26.74, 47.64) * mm, v(27.37, 47.42) * mm, v(28.3, 47.05) * mm, v(28.83, 46.75) * mm, v(29.46, 46.32) * mm, v(29.88, 45.98) * mm, v(30.46, 45.48) * mm, v(30.88, 45.06) * mm, v(31.23, 44.72) * mm, v(31.6, 44.38) * mm, v(31.82, 44.05) * mm, v(32, 43.72) * mm, v(32.06, 43.46) * mm, v(32.04, 43.24) * mm, v(31.95, 43.15) * mm, v(31.81, 43.1) * mm, v(31.54, 43.2) * mm, v(31.24, 43.41) * mm, v(30.82, 43.77) * mm, v(30.4, 44.16) * mm, v(30, 44.55) * mm, v(29.6, 44.92) * mm, v(29.14, 45.31) * mm, v(28.65, 45.7) * mm, v(27.96, 46.13) * mm, v(27.34, 46.5) * mm, v(26.91, 46.7) * mm, v(26.32, 46.92) * mm, v(25.79, 47.04) * mm, v(25.13, 47.07) * mm, v(24.26, 47.04) * mm, v(23.53, 46.86) * mm, v(22.56, 46.52) * mm, v(22.03, 46.24) * mm, v(21.37, 45.97) * mm, v(20.6, 45.78) * mm, v(19.78, 45.64) * mm, v(18.77, 45.4) * mm, v(18.04, 45.31) * mm, v(17.6, 45.3) * mm, v(17.22, 45.34) * mm, v(16.96, 45.54) * mm, v(16.98, 45.68) * mm, v(17.24, 45.89) * mm, v(17.73, 45.99) * mm, v(18.51, 45.99) * mm, v(19.04, 46) * mm, v(19.58, 46.14) * mm, v(20.32, 46.34) * mm, v(20.96, 46.6) * mm, v(21.66, 46.88) * mm, v(22.34, 47.2) * mm, v(22.92, 47.45) * mm, v(23.39, 47.64) * mm, v(23.8, 47.73) * mm, v(24.25, 47.76) * mm]});
            skFitSpline(sketch, "E20", {"points": [v(18.48, 47.5) * mm, v(18.8, 47.67) * mm, v(19.18, 47.81) * mm, v(19.65, 47.85) * mm, v(20.43, 47.86) * mm, v(21.02, 47.85) * mm, v(21.41, 47.72) * mm, v(21.64, 47.6) * mm, v(21.69, 47.5) * mm, v(21.58, 47.38) * mm, v(21.23, 47.2) * mm, v(20.78, 47) * mm, v(20.17, 46.81) * mm, v(19.85, 46.73) * mm, v(19.31, 46.83) * mm, v(18.85, 47.01) * mm, v(18.54, 47.17) * mm, v(18.38, 47.3) * mm, v(18.48, 47.5) * mm]});
            skFitSpline(sketch, "E21", {"points": [v(23.84, 45.25) * mm, v(24.2, 45.4) * mm, v(24.74, 45.5) * mm, v(25.55, 45.55) * mm, v(25.92, 45.41) * mm, v(26.17, 45.29) * mm, v(26.24, 45.17) * mm, v(26.15, 44.9) * mm, v(25.88, 44.41) * mm, v(25.75, 44.2) * mm, v(25.56, 44.08) * mm, v(25.3, 44.13) * mm, v(24.86, 44.36) * mm, v(24.4, 44.64) * mm, v(23.93, 44.94) * mm, v(23.76, 45.08) * mm, v(23.74, 45.16) * mm, v(23.84, 45.25) * mm]});
            skFitSpline(sketch, "E22", {"points": [v(28.26, 42.74) * mm, v(28.98, 42.3) * mm, v(29.8, 41.84) * mm, v(30.6, 41.42) * mm, v(31.26, 41.1) * mm, v(31.8, 40.8) * mm, v(32.03, 40.7) * mm, v(32.22, 40.7) * mm, v(32.6, 40.85) * mm, v(32.95, 41.04) * mm, v(33.03, 41.12) * mm, v(33, 41.22) * mm, v(32.63, 41.51) * mm, v(31.88, 42) * mm, v(31.3, 42.4) * mm, v(30.9, 42.72) * mm, v(30.58, 42.98) * mm, v(29.8, 43.46) * mm, v(28.94, 43.95) * mm, v(28.25, 44.38) * mm, v(28.08, 44.46) * mm, v(27.93, 44.4) * mm, v(27.8, 44.04) * mm, v(27.7, 43.7) * mm, v(27.62, 43.4) * mm, v(27.62, 43.2) * mm, v(27.87, 42.99) * mm, v(28.26, 42.74) * mm]});
            skFitSpline(sketch, "E23", {"points": [v(12.19, 45.76) * mm, v(13.2, 45.27) * mm, v(14.31, 44.8) * mm, v(15.22, 44.4) * mm, v(16.9, 43.64) * mm, v(17.01, 43.57) * mm, v(17.03, 43.18) * mm, v(17.06, 42.19) * mm, v(17.14, 41.3) * mm, v(17.27, 40.59) * mm, v(17.4, 39.97) * mm, v(17.39, 39.77) * mm, v(17.25, 39.95) * mm, v(17.12, 40.38) * mm, v(17.02, 40.92) * mm, v(16.92, 41.54) * mm, v(16.8, 42.27) * mm, v(16.72, 42.51) * mm, v(16.6, 42.65) * mm, v(16.42, 42.62) * mm, v(16.32, 42.49) * mm, v(16.24, 42.35) * mm, v(16.16, 42.28) * mm, v(15.94, 42.3) * mm, v(15.66, 42.43) * mm, v(15.26, 42.6) * mm, v(14.61, 42.94) * mm, v(13.85, 43.34) * mm, v(12.96, 43.88) * mm, v(11.98, 44.48) * mm, v(11.35, 44.87) * mm, v(10.88, 45.2) * mm, v(10.2, 45.8) * mm, v(9.49, 46.5) * mm, v(9, 47) * mm, v(8.57, 47.42) * mm, v(8.42, 47.64) * mm, v(8.35, 47.82) * mm, v(8.42, 47.88) * mm, v(8.6, 47.79) * mm, v(9.1, 47.47) * mm, v(9.93, 47) * mm, v(10.56, 46.63) * mm, v(11.59, 46.12) * mm, v(12.19, 45.76) * mm]});
            skFitSpline(sketch, "E24", {"points": [v(18.95, 41.87) * mm, v(19.39, 40.32) * mm, v(19.6, 39.68) * mm, v(19.87, 39) * mm, v(20.21, 38.37) * mm, v(20.72, 37.84) * mm, v(21.37, 37.25) * mm, v(22.09, 36.64) * mm, v(22.5, 36.28) * mm, v(22.72, 36.06) * mm, v(22.7, 35.94) * mm, v(22.51, 35.9) * mm, v(22.22, 35.92) * mm, v(21.82, 36.05) * mm, v(21.37, 36.25) * mm, v(20.73, 36.65) * mm, v(20.44, 36.9) * mm, v(20.14, 37.3) * mm, v(19.77, 37.93) * mm, v(19.44, 38.5) * mm, v(19.02, 39.38) * mm, v(18.47, 40.65) * mm, v(18.27, 41.32) * mm, v(18.15, 41.95) * mm, v(18.1, 42.52) * mm, v(18.11, 42.69) * mm, v(18.17, 42.74) * mm, v(18.28, 42.7) * mm, v(18.45, 42.54) * mm, v(18.69, 42.3) * mm, v(18.95, 41.87) * mm]});
            skFitSpline(sketch, "E25", {"points": [v(20.46, 41.78) * mm, v(22.43, 40.78) * mm, v(23.78, 40.15) * mm, v(25.12, 39.52) * mm, v(26.05, 39.15) * mm, v(26.88, 38.88) * mm, v(27.4, 38.78) * mm, v(28.03, 38.8) * mm, v(28.65, 38.92) * mm, v(29.32, 39.11) * mm, v(29.76, 39.25) * mm, v(30.3, 39.3) * mm, v(30.45, 39.26) * mm, v(30.48, 39.14) * mm, v(30.41, 39.07) * mm, v(30.32, 39.04) * mm, v(30.3, 38.91) * mm, v(30.3, 37.54) * mm, v(30.22, 36.8) * mm, v(30.12, 36.5) * mm, v(29.94, 36.2) * mm, v(29.6, 35.88) * mm, v(29.18, 35.7) * mm, v(28.64, 35.48) * mm, v(28.03, 35.24) * mm, v(27.41, 35.03) * mm, v(27.15, 35) * mm, v(26.92, 35.04) * mm, v(26.55, 35.4) * mm, v(26.31, 35.7) * mm, v(26.06, 36.12) * mm, v(25.9, 36.55) * mm, v(25.64, 37.67) * mm, v(25.57, 37.98) * mm, v(25.53, 38.07) * mm, v(25.23, 38.14) * mm, v(24.7, 38.17) * mm, v(24.28, 38.23) * mm, v(23.3, 38.35) * mm, v(22.22, 38.64) * mm, v(21.43, 39) * mm, v(20.99, 39.13) * mm, v(20.57, 39.38) * mm, v(20.17, 39.7) * mm, v(19.87, 40.07) * mm, v(19.67, 40.79) * mm, v(19.48, 41.56) * mm, v(19.3, 42.05) * mm, v(19.2, 42.3) * mm, v(19.17, 42.39) * mm, v(19.27, 42.43) * mm, v(19.78, 42.15) * mm, v(20.46, 41.78) * mm]});
            skFitSpline(sketch, "E26", {"points": [v(36.36, 39) * mm, v(38.33, 37.67) * mm, v(40.12, 36.55) * mm, v(41.31, 35.81) * mm, v(42.6, 34.97) * mm, v(43.43, 34.48) * mm, v(44.06, 34.19) * mm, v(44.43, 34) * mm, v(44.51, 33.9) * mm, v(44.46, 33.83) * mm, v(44.12, 33.85) * mm, v(43.42, 33.95) * mm, v(42.46, 34.04) * mm, v(41.32, 34.17) * mm, v(40.75, 34.31) * mm, v(40.35, 34.43) * mm, v(39.97, 34.47) * mm, v(39.72, 34.61) * mm, v(38.87, 35.24) * mm, v(38.13, 35.65) * mm, v(37.63, 35.94) * mm, v(37.07, 36.27) * mm, v(35.31, 37.36) * mm, v(33.74, 38.27) * mm, v(31.69, 39.35) * mm, v(30.83, 39.6) * mm, v(29.82, 39.7) * mm, v(29.28, 39.6) * mm, v(28.58, 39.3) * mm, v(28.03, 39.23) * mm, v(27.18, 39.32) * mm, v(25.9, 39.7) * mm, v(22.72, 41.19) * mm, v(20.45, 42.3) * mm, v(20.17, 42.54) * mm, v(18.69, 43.34) * mm, v(17.35, 43.97) * mm, v(15.01, 45) * mm, v(13.24, 45.72) * mm, v(11.79, 46.45) * mm, v(10.36, 47.2) * mm, v(9.26, 47.93) * mm, v(9.16, 48.02) * mm, v(9.15, 48.08) * mm, v(9.29, 48.04) * mm, v(9.6, 47.9) * mm, v(10.1, 47.71) * mm, v(10.83, 47.43) * mm, v(11.47, 47.24) * mm, v(12.3, 47.08) * mm, v(13.14, 47.01) * mm, v(14.1, 47) * mm, v(15.42, 47.03) * mm, v(16.66, 47.2) * mm, v(16.93, 47.25) * mm, v(17.3, 47.1) * mm, v(17.8, 46.92) * mm, v(18.15, 46.72) * mm, v(18.27, 46.64) * mm, v(18.25, 46.58) * mm, v(18.17, 46.55) * mm, v(17.83, 46.55) * mm, v(16.27, 46.54) * mm, v(15.6, 46.1) * mm, v(15.54, 45.83) * mm, v(15.6, 45.28) * mm, v(15.9, 44.99) * mm, v(16.22, 44.76) * mm, v(16.58, 44.55) * mm, v(17.09, 44.4) * mm, v(17.62, 44.3) * mm, v(18.36, 44.22) * mm, v(18.95, 44.2) * mm, v(19.39, 44.2) * mm, v(20.72, 44.32) * mm, v(21.94, 44.58) * mm, v(22.62, 44.73) * mm, v(22.83, 44.77) * mm, v(23.3, 44.6) * mm, v(23.89, 44.24) * mm, v(24.4, 44) * mm, v(25.04, 43.64) * mm, v(25.47, 43.43) * mm, v(25.69, 43.37) * mm, v(25.9, 43.4) * mm, v(26.12, 43.62) * mm, v(26.43, 44.08) * mm, v(26.78, 44.65) * mm, v(27.03, 44.92) * mm, v(27.22, 44.98) * mm, v(27.4, 44.92) * mm, v(27.49, 44.77) * mm, v(27.46, 44.57) * mm, v(27.27, 44.13) * mm, v(27.1, 43.62) * mm, v(27, 43.2) * mm, v(27.04, 42.93) * mm, v(27.27, 42.68) * mm, v(29.18, 41.32) * mm, v(30.6, 40.55) * mm, v(31.47, 40.07) * mm, v(31.77, 40.02) * mm, v(32.05, 40.07) * mm, v(32.5, 40.27) * mm, v(33.2, 40.55) * mm, v(33.41, 40.6) * mm, v(33.6, 40.63) * mm, v(33.95, 40.54) * mm, v(34.37, 40.28) * mm, v(35.28, 39.65) * mm, v(36.36, 39) * mm]});
            skFitSpline(sketch, "E27", {"points": [v(32.54, 35.77) * mm, v(31.6, 36.24) * mm, v(30.91, 36.55) * mm, v(30.81, 36.6) * mm, v(30.78, 36.88) * mm, v(30.78, 37.43) * mm, v(30.73, 38.37) * mm, v(30.7, 38.73) * mm, v(30.72, 38.82) * mm, v(31, 38.78) * mm, v(31.93, 38.43) * mm, v(32.95, 38.03) * mm, v(34, 37.5) * mm, v(36.94, 35.75) * mm, v(38.5, 34.76) * mm, v(38.91, 34.55) * mm, v(39, 34.47) * mm, v(38.97, 34.39) * mm, v(38.79, 34.37) * mm, v(38.25, 34.37) * mm, v(37.52, 34.52) * mm, v(36.52, 34.74) * mm, v(35.76, 35.06) * mm, v(34.82, 35.5) * mm, v(34.06, 35.99) * mm, v(33.95, 36.09) * mm, v(33.87, 36.12) * mm, v(33.77, 36.08) * mm, v(33.71, 35.88) * mm, v(33.74, 35.39) * mm, v(33.76, 35.15) * mm, v(33.72, 35.06) * mm, v(33.6, 35.06) * mm, v(33.26, 35.29) * mm, v(32.78, 35.61) * mm, v(32.54, 35.77) * mm]});
            skFitSpline(sketch, "E28", {"points": [v(27.65, 34.61) * mm, v(29.68, 34) * mm, v(30.81, 33.66) * mm, v(31.59, 33.34) * mm, v(32.22, 33.04) * mm, v(32.68, 32.75) * mm, v(32.91, 32.57) * mm, v(32.93, 32.46) * mm, v(32.72, 32.44) * mm, v(32.4, 32.51) * mm, v(31.8, 32.64) * mm, v(30.51, 33.01) * mm, v(29.66, 33.31) * mm, v(28.81, 33.65) * mm, v(28, 34.06) * mm, v(27.54, 34.38) * mm, v(27.44, 34.52) * mm, v(27.47, 34.61) * mm, v(27.65, 34.61) * mm]});
            skFitSpline(sketch, "E29", {"points": [v(38.55, 32.72) * mm, v(39.1, 32.32) * mm, v(39.5, 32.14) * mm, v(39.73, 32.07) * mm, v(40.01, 32.2) * mm, v(40.18, 32.45) * mm, v(40.34, 32.8) * mm, v(40.42, 33) * mm, v(40.42, 33.23) * mm, v(40.33, 33.32) * mm, v(40.23, 33.25) * mm, v(40.18, 33.08) * mm, v(40.13, 32.93) * mm, v(39.91, 32.88) * mm, v(39.52, 32.96) * mm, v(39.11, 33.1) * mm, v(38.68, 33.18) * mm, v(37.97, 33.24) * mm, v(37.89, 33.23) * mm, v(38.02, 33.1) * mm, v(38.55, 32.72) * mm]});
            skFitSpline(sketch, "E30", {"points": [v(43.74, 31.46) * mm, v(44.5, 31) * mm, v(45.2, 30.54) * mm, v(45.87, 30.09) * mm, v(46.25, 29.8) * mm, v(46.4, 29.57) * mm, v(46.43, 29.22) * mm, v(46.1, 28.38) * mm, v(45.74, 28) * mm, v(45.63, 27.92) * mm, v(45.4, 27.91) * mm, v(45.2, 28) * mm, v(44.76, 28.3) * mm, v(44.13, 28.72) * mm, v(43.3, 29.33) * mm, v(42.6, 29.8) * mm, v(42.11, 30.2) * mm, v(42.04, 30.27) * mm, v(42.21, 30.51) * mm, v(42.69, 31.07) * mm, v(42.9, 31.37) * mm, v(42.98, 31.65) * mm, v(43.03, 31.8) * mm, v(43.2, 31.78) * mm, v(43.74, 31.46) * mm]});
            skFitSpline(sketch, "E31", {"points": [v(64.47, 26.91) * mm, v(66.25, 26.24) * mm, v(67.38, 25.86) * mm, v(68.23, 25.6) * mm, v(68.57, 25.52) * mm, v(68.66, 25.43) * mm, v(68.58, 25.24) * mm, v(68.26, 24.94) * mm, v(67.77, 24.42) * mm, v(67.64, 24.1) * mm, v(67.53, 23.92) * mm, v(67.15, 23.77) * mm, v(66.03, 23.47) * mm, v(64.34, 23.12) * mm, v(62.81, 22.9) * mm, v(61.62, 22.77) * mm, v(59.86, 22.7) * mm, v(58.66, 22.84) * mm, v(57.52, 23.17) * mm, v(55.45, 24.23) * mm, v(54.32, 25) * mm, v(53.42, 25.54) * mm, v(52.34, 26.46) * mm, v(51.23, 27.34) * mm, v(50.49, 27.82) * mm, v(50.02, 28.13) * mm, v(49.83, 28.14) * mm, v(49.65, 28) * mm, v(49.38, 27.57) * mm, v(49.06, 27.06) * mm, v(48.32, 26.14) * mm, v(47.88, 25.77) * mm, v(47.34, 25.46) * mm, v(46.84, 25.24) * mm, v(46.69, 25.11) * mm, v(46.7, 24.94) * mm, v(46.96, 24.76) * mm, v(48, 24.16) * mm, v(48.96, 23.7) * mm, v(49.71, 23.4) * mm, v(51.3, 22.68) * mm, v(52.9, 22.14) * mm, v(54.54, 21.66) * mm, v(55.65, 21.29) * mm, v(56.6, 21.02) * mm, v(57.3, 20.9) * mm, v(57.89, 20.87) * mm, v(58.07, 20.83) * mm, v(58.06, 20.64) * mm, v(57.88, 20.2) * mm, v(57.68, 19.64) * mm, v(57.6, 19.44) * mm, v(57.69, 19.25) * mm, v(58, 19.01) * mm, v(58.43, 18.77) * mm, v(58.78, 18.6) * mm, v(58.93, 18.44) * mm, v(58.85, 18.32) * mm, v(58.46, 18.32) * mm, v(57.94, 18.36) * mm, v(57.22, 18.45) * mm, v(56.63, 18.58) * mm, v(55.2, 19.08) * mm, v(54.33, 19.48) * mm, v(53.61, 19.85) * mm, v(53.19, 20.14) * mm, v(52.75, 20.42) * mm, v(52.34, 20.6) * mm, v(51.43, 20.97) * mm, v(50.36, 21.47) * mm, v(49.5, 21.97) * mm, v(48.97, 22.32) * mm, v(48.47, 22.7) * mm, v(48.02, 23.08) * mm, v(47.25, 23.75) * mm, v(46.73, 24.37) * mm, v(46.44, 24.85) * mm, v(46.36, 24.89) * mm, v(45.83, 24.9) * mm, v(43.65, 24.9) * mm, v(42.6, 24.9) * mm, v(42.5, 24.87) * mm, v(42.26, 24.67) * mm, v(42.06, 24.48) * mm, v(41.74, 24.29) * mm, v(41.55, 24.1) * mm, v(41.55, 23.95) * mm, v(41.74, 23.76) * mm, v(41.96, 23.54) * mm, v(42.28, 23.3) * mm, v(43.3, 22.62) * mm, v(43.8, 22.27) * mm, v(44.2, 21.98) * mm, v(44.63, 21.7) * mm, v(45.54, 20.8) * mm, v(45.89, 20.43) * mm, v(46.39, 19.86) * mm, v(46.52, 19.62) * mm, v(46.64, 19.43) * mm, v(46.74, 19.07) * mm, v(46.72, 18.79) * mm, v(46.55, 18.67) * mm, v(46.17, 18.6) * mm, v(43.39, 18.15) * mm, v(39.38, 17.47) * mm, v(37.15, 17.05) * mm, v(36.4, 17.05) * mm, v(35.79, 17.13) * mm, v(34.82, 17.4) * mm, v(33.7, 17.87) * mm, v(33.11, 18.15) * mm, v(32.54, 18.47) * mm, v(31.12, 19.35) * mm, v(30.84, 19.59) * mm, v(30.73, 19.73) * mm, v(30.57, 20.02) * mm, v(30.5, 20.34) * mm, v(30.33, 21.1) * mm, v(30.27, 21.48) * mm, v(30.33, 21.7) * mm, v(30.44, 21.79) * mm, v(30.6, 21.8) * mm, v(30.77, 21.74) * mm, v(31.1, 21.58) * mm, v(31.44, 21.44) * mm, v(31.9, 21.22) * mm, v(32.36, 20.98) * mm, v(32.98, 20.62) * mm, v(34.13, 19.92) * mm, v(35.61, 19.14) * mm, v(36.23, 18.84) * mm, v(36.87, 18.52) * mm, v(37.97, 18.04) * mm, v(38.23, 17.95) * mm, v(38.68, 17.95) * mm, v(39.72, 18.14) * mm, v(40.37, 18.34) * mm, v(40.8, 18.49) * mm, v(41.13, 18.68) * mm, v(41.24, 18.77) * mm, v(41.26, 18.93) * mm, v(41.13, 19.08) * mm, v(40.85, 19.27) * mm, v(40.33, 19.51) * mm, v(39.84, 19.68) * mm, v(39.49, 19.83) * mm, v(39.05, 20.1) * mm, v(38.76, 20.32) * mm, v(38.46, 20.57) * mm, v(37.31, 21.6) * mm, v(36.94, 22) * mm, v(36.01, 22.92) * mm, v(35.46, 23.52) * mm, v(35.14, 23.87) * mm, v(34.7, 24.36) * mm, v(33.67, 25.45) * mm, v(33.26, 26) * mm, v(32.54, 26.9) * mm, v(32.02, 27.64) * mm, v(31.27, 28.78) * mm, v(30.9, 29.48) * mm, v(30.6, 30.15) * mm, v(30.24, 30.95) * mm, v(29.96, 31.52) * mm, v(29.8, 31.7) * mm, v(29.37, 32.03) * mm, v(28.65, 32.32) * mm, v(27.54, 32.85) * mm, v(26.65, 33.32) * mm, v(26.15, 33.68) * mm, v(25.37, 34.25) * mm, v(24.65, 34.89) * mm, v(24.28, 35.27) * mm, v(23.67, 35.95) * mm, v(23.15, 36.45) * mm, v(22.36, 37.06) * mm, v(21.98, 37.39) * mm, v(21.31, 37.9) * mm, v(20.99, 38.17) * mm, v(20.83, 38.35) * mm, v(20.83, 38.44) * mm, v(21.03, 38.39) * mm, v(21.3, 38.23) * mm, v(21.7, 38) * mm, v(22.14, 37.78) * mm, v(22.67, 37.54) * mm, v(23.3, 37.32) * mm, v(23.97, 37.04) * mm, v(24.51, 36.76) * mm, v(25.15, 36.36) * mm, v(25.7, 35.84) * mm, v(26.1, 35.24) * mm, v(26.4, 34.92) * mm, v(26.77, 34.58) * mm, v(27.12, 34.22) * mm, v(27.67, 33.72) * mm, v(28, 33.48) * mm, v(28.33, 33.32) * mm, v(28.81, 33.13) * mm, v(29.52, 32.88) * mm, v(30.3, 32.6) * mm, v(31.92, 32.14) * mm, v(32.8, 31.94) * mm, v(33.76, 31.78) * mm, v(35.4, 31.54) * mm, v(36.87, 31.46) * mm, v(37.15, 31.53) * mm, v(37.24, 31.6) * mm, v(37.35, 31.57) * mm, v(37.49, 31.4) * mm, v(37.65, 31.09) * mm, v(37.88, 30.93) * mm, v(38.2, 30.82) * mm, v(38.62, 30.76) * mm, v(39.67, 30.77) * mm, v(40.3, 30.84) * mm, v(41.36, 31.12) * mm, v(42.04, 31.53) * mm, v(42.32, 31.94) * mm, v(42.38, 32.45) * mm, v(42.25, 32.8) * mm, v(42.05, 33.15) * mm, v(41.8, 33.4) * mm, v(41.7, 33.56) * mm, v(41.72, 33.65) * mm, v(41.98, 33.7) * mm, v(42.41, 33.6) * mm, v(43.57, 33.47) * mm, v(44.2, 33.4) * mm, v(44.82, 33.24) * mm, v(45.14, 33.04) * mm, v(45.45, 32.82) * mm, v(45.78, 32.51) * mm, v(45.97, 32.27) * mm, v(46.13, 31.99) * mm, v(46.26, 31.73) * mm, v(46.4, 30.94) * mm, v(46.45, 30.5) * mm, v(46.4, 30.34) * mm, v(46.3, 30.34) * mm, v(46.17, 30.44) * mm, v(45.77, 30.71) * mm, v(45.32, 31.04) * mm, v(44.23, 31.76) * mm, v(43.67, 32.08) * mm, v(43.2, 32.28) * mm, v(43.06, 32.3) * mm, v(42.84, 32.25) * mm, v(42.76, 32.13) * mm, v(42.63, 31.82) * mm, v(42.33, 31.19) * mm, v(41.89, 30.77) * mm, v(41.57, 30.65) * mm, v(41.13, 30.58) * mm, v(40.8, 30.5) * mm, v(40.27, 30.24) * mm, v(39.91, 29.97) * mm, v(39.76, 29.82) * mm, v(39.76, 29.66) * mm, v(39.9, 29.38) * mm, v(40.22, 28.86) * mm, v(40.48, 28.54) * mm, v(40.68, 28.28) * mm, v(40.74, 28.06) * mm, v(40.82, 27.34) * mm, v(40.98, 26.76) * mm, v(41.27, 26.4) * mm, v(41.7, 26.17) * mm, v(42.4, 25.82) * mm, v(42.92, 25.65) * mm, v(43.66, 25.57) * mm, v(45.43, 25.57) * mm, v(46.16, 25.66) * mm, v(47, 26) * mm, v(47.74, 26.43) * mm, v(48.64, 27.17) * mm, v(49.33, 27.87) * mm, v(49.67, 28.3) * mm, v(50, 29.24) * mm, v(50.34, 30.45) * mm, v(50.47, 31.21) * mm, v(50.52, 31.46) * mm, v(50.56, 31.5) * mm, v(50.67, 31.44) * mm, v(50.81, 31.24) * mm, v(51, 31) * mm, v(51.25, 30.76) * mm, v(51.43, 30.61) * mm, v(51.72, 30.58) * mm, v(52.06, 30.65) * mm, v(52.22, 30.7) * mm, v(52.56, 30.7) * mm, v(52.96, 30.51) * mm, v(53.3, 30.27) * mm, v(54.17, 29.79) * mm, v(54.79, 29.57) * mm, v(55.5, 29.29) * mm, v(56.05, 29.14) * mm, v(56.65, 28.98) * mm, v(57.08, 28.86) * mm, v(57.36, 28.63) * mm, v(57.78, 27.92) * mm, v(58.18, 27.24) * mm, v(58.7, 26.57) * mm, v(59.24, 25.94) * mm, v(60.26, 24.89) * mm, v(60.88, 24.37) * mm, v(61.19, 24.17) * mm, v(61.75, 23.95) * mm, v(62.21, 23.92) * mm, v(63.54, 23.9) * mm, v(64.27, 24.14) * mm, v(64.4, 24.25) * mm, v(64.38, 24.38) * mm, v(64.09, 24.63) * mm, v(63.67, 24.93) * mm, v(63.08, 25.41) * mm, v(62.7, 25.79) * mm, v(62.33, 26.16) * mm, v(61.9, 26.73) * mm, v(61.45, 27.38) * mm, v(61.08, 28.04) * mm, v(61.01, 28.18) * mm, v(61.06, 28.24) * mm, v(61.18, 28.24) * mm, v(61.4, 28.13) * mm, v(61.9, 27.9) * mm, v(62.48, 27.68) * mm, v(62.9, 27.52) * mm, v(64.47, 26.91) * mm]});
            skFitSpline(sketch, "E32", {"points": [v(50.57, 27) * mm, v(50.94, 26.67) * mm, v(51.07, 26.54) * mm, v(50.96, 26.3) * mm, v(50.77, 25.9) * mm, v(50.48, 25.53) * mm, v(49.66, 24.88) * mm, v(49.08, 24.61) * mm, v(48.6, 24.52) * mm, v(48.13, 24.63) * mm, v(47.9, 24.8) * mm, v(47.87, 24.88) * mm, v(48.1, 25.13) * mm, v(48.63, 25.55) * mm, v(49.11, 26) * mm, v(49.5, 26.38) * mm, v(49.9, 26.93) * mm, v(50.06, 27.17) * mm, v(50.15, 27.25) * mm, v(50.24, 27.28) * mm, v(50.44, 27.15) * mm, v(50.57, 27) * mm]});
            skFitSpline(sketch, "E33", {"points": [v(52.16, 25.77) * mm, v(52.44, 25.52) * mm, v(52.57, 25.32) * mm, v(52.57, 25.12) * mm, v(52.31, 24.75) * mm, v(51.75, 24.15) * mm, v(51.24, 23.74) * mm, v(50.94, 23.58) * mm, v(50.67, 23.58) * mm, v(50.42, 23.69) * mm, v(50.18, 23.85) * mm, v(50.06, 23.94) * mm, v(50.05, 24) * mm, v(50.18, 24.11) * mm, v(50.56, 24.39) * mm, v(50.92, 24.76) * mm, v(51.23, 25.12) * mm, v(51.53, 25.49) * mm, v(51.75, 25.82) * mm, v(51.8, 25.92) * mm, v(51.86, 25.99) * mm, v(51.98, 25.93) * mm, v(52.16, 25.77) * mm]});
            skFitSpline(sketch, "E34", {"points": [v(54.02, 24.3) * mm, v(54.34, 24.02) * mm, v(54.5, 23.84) * mm, v(54.5, 23.6) * mm, v(54.41, 23.35) * mm, v(54.2, 23) * mm, v(53.97, 22.69) * mm, v(53.74, 22.49) * mm, v(53.56, 22.4) * mm, v(53.34, 22.42) * mm, v(53.06, 22.53) * mm, v(52.52, 22.72) * mm, v(52.06, 22.9) * mm, v(51.86, 23) * mm, v(51.76, 23.04) * mm, v(51.77, 23.14) * mm, v(52.02, 23.33) * mm, v(52.5, 23.67) * mm, v(52.88, 23.98) * mm, v(53.24, 24.34) * mm, v(53.4, 24.52) * mm, v(53.5, 24.57) * mm, v(53.68, 24.52) * mm, v(53.86, 24.41) * mm, v(54.02, 24.3) * mm]});
            skFitSpline(sketch, "E35", {"points": [v(45.13, 22.53) * mm, v(46.85, 21.78) * mm, v(48.69, 20.94) * mm, v(49.95, 20.41) * mm, v(51.6, 19.72) * mm, v(53.69, 18.82) * mm, v(54.79, 18.32) * mm, v(55.08, 18.18) * mm, v(55.14, 18.1) * mm, v(54.96, 18.08) * mm, v(54.65, 18.21) * mm, v(53.92, 18.46) * mm, v(52.95, 18.85) * mm, v(51.9, 19.25) * mm, v(50.42, 19.8) * mm, v(48.54, 20.62) * mm, v(46.14, 21.82) * mm, v(44.75, 22.55) * mm, v(44.34, 22.78) * mm, v(44.3, 22.85) * mm, v(44.43, 22.87) * mm, v(44.68, 22.76) * mm, v(44.95, 22.63) * mm, v(45.13, 22.53) * mm]});
            skFitSpline(sketch, "E36", {"points": [v(33.74, 21.7) * mm, v(36.06, 20.6) * mm, v(36.95, 20.22) * mm, v(38.42, 19.5) * mm, v(39.19, 19.14) * mm, v(39.36, 19.02) * mm, v(39.28, 18.89) * mm, v(38.98, 18.8) * mm, v(38.59, 18.87) * mm, v(38.22, 18.98) * mm, v(37.27, 19.32) * mm, v(36.36, 19.74) * mm, v(35.34, 20.26) * mm, v(34.45, 20.7) * mm, v(33.24, 21.38) * mm, v(30.32, 22.9) * mm, v(28.21, 23.94) * mm, v(28.02, 24.1) * mm, v(28.02, 24.2) * mm, v(28.17, 24.16) * mm, v(28.58, 24) * mm, v(29.92, 23.38) * mm, v(32.9, 22.08) * mm, v(33.74, 21.7) * mm]});
            skFitSpline(sketch, "E37", {"points": [v(27.14, 25.46) * mm, v(28.37, 24.78) * mm, v(29.56, 24.13) * mm, v(30.59, 23.64) * mm, v(31.9, 23.03) * mm, v(32.45, 22.8) * mm, v(32.56, 22.8) * mm, v(32.55, 22.89) * mm, v(32.31, 23.07) * mm, v(31.72, 23.54) * mm, v(31.14, 23.96) * mm, v(30.48, 24.5) * mm, v(30.1, 24.9) * mm, v(29.83, 25.3) * mm, v(29.6, 25.66) * mm, v(29.17, 26.12) * mm, v(28.5, 26.57) * mm, v(28.28, 26.73) * mm, v(28.17, 26.8) * mm, v(28.03, 26.75) * mm, v(27.74, 26.57) * mm, v(27.39, 26.4) * mm, v(27.1, 26.31) * mm, v(26.8, 26.36) * mm, v(25.77, 26.76) * mm, v(25.16, 27.06) * mm, v(24.99, 27.08) * mm, v(24.95, 27) * mm, v(25.1, 26.84) * mm, v(25.44, 26.52) * mm, v(25.97, 26.18) * mm, v(26.38, 25.92) * mm, v(27.14, 25.46) * mm]});
            skFitSpline(sketch, "E38", {"points": [v(24.83, 28.9) * mm, v(26.5, 28.03) * mm, v(27.3, 27.6) * mm, v(27.57, 27.34) * mm, v(27.53, 27.03) * mm, v(27.34, 26.9) * mm, v(27.08, 26.95) * mm, v(26.34, 27.28) * mm, v(25.01, 27.91) * mm, v(23.52, 28.67) * mm, v(23.1, 28.97) * mm, v(22.83, 29.26) * mm, v(22.57, 29.7) * mm, v(22.5, 29.94) * mm, v(22.6, 30) * mm, v(23.06, 29.78) * mm, v(23.8, 29.4) * mm, v(24.83, 28.9) * mm]});
            skSolve(sketch);
        }
        {
            var Q0;
            {var subQ5=sQuery(id+"F0.wireOp",EDGE,"E1");Q0=makeQuery(id+"F0.imprint","IMPRINT",FACE,{"disambiguationData":[TD([[makeQuery(id+"F0.imprint","IMPRINT",EDGE,{"derivedFrom":subQ5}),-1.0]])]});}
            extrude(context, id + "F1", {"entities" : qUnion([Q0]), "depth" : 6.35 * mm, "offsetDistance" : 25.4 * mm});
        }
    });
